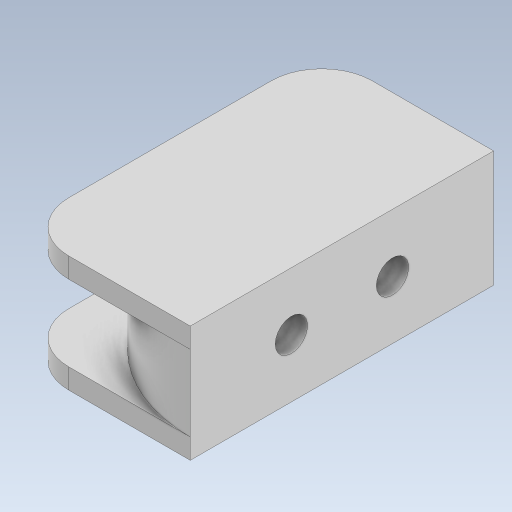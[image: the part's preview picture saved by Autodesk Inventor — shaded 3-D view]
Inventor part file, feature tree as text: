
AUTODESK INVENTOR PART (.ipt)
format: ipt  version: 2023.5 (Build 275446000, 446)  size: 155,136 bytes
history: native  units: mm
features: extrude x5, sketch x4, plane x1, fillet x1
ambient origin geometry x8: Origin, YZ Plane, XZ Plane, XY Plane, X Axis, Y Axis, Z Axis, Center Point
bodies: Body1 (feature_tree)
feature tree (11):
  extrude  "Extrusion2"  Depth=11.5mm TaperAngle=0.0deg
  extrude  "Extrusion3"  Depth=2.0mm TaperAngle=0.0deg
  extrude  "Extrusion4"  Depth=10.0mm
  plane  "Work Plane1"
  sketch  "Sketch5"  dims[d12=3.2mm d13=10.0mm d14=5.5mm d15=5.5mm d16=15.0mm d17=0.0mm d18=9.0mm d19=0.0mm d20=5.0mm]
  extrude  "Extrusion5"  Depth=10.0mm
  extrude  "Extrusion6"  Depth=5.0mm
  fillet  "Fillet1"  Radius=5.5mm
  sketch  "Sketch1"  dims[d0=30.0mm d3=11.5mm d4=0.0mm]
  sketch  "Sketch2"  dims[d5=2.0mm d6=0.0mm d7=2.0mm d8=0.0mm]
  sketch  "Sketch3"  dims[d10=3.2mm d11=10.0mm]
